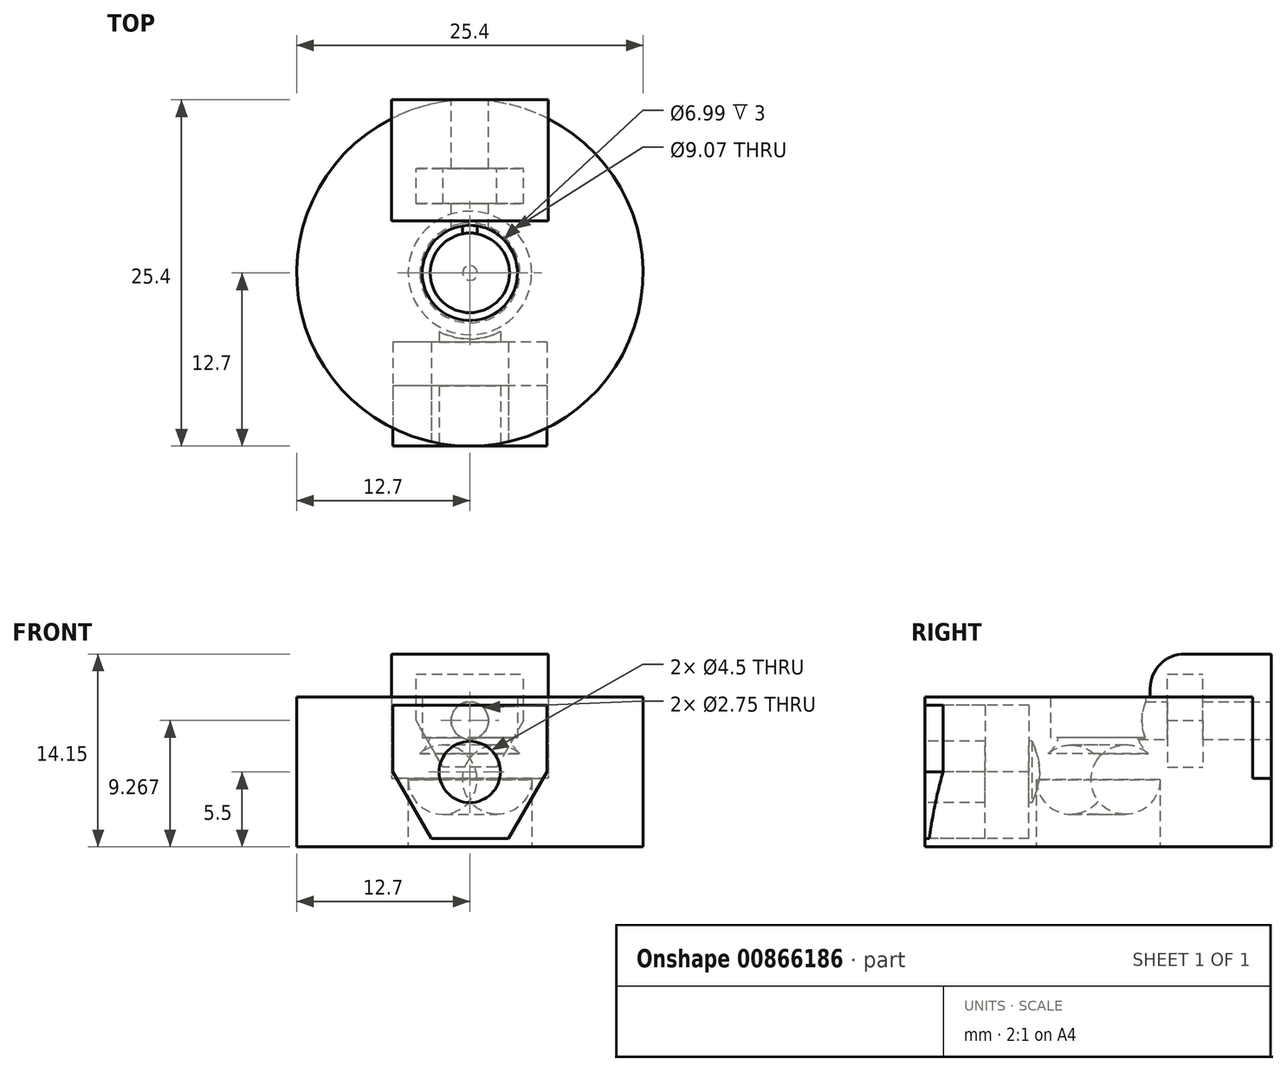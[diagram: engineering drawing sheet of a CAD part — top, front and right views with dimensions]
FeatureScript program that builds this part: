
annotation { "Feature Type Name" : "Feature", "Feature Type Description" : "" }
export const myFeature = defineFeature(function(context is Context, id is Id, definition is map)
    precondition{}
    {
        {
            var Q0;
            Q0=qCreatedBy(makeId("Top.planeOp"),FACE);
            var sketch = newSketch(context, id + "F0", { "sketchPlane" : qUnion([Q0])});
            skCircle(sketch, "E0", {"center": v(0, 0) * mm, "radius": 3.5 * mm});
            skCircle(sketch, "E1", {"center": v(0, 0) * mm, "radius": 12.7 * mm});
            skSolve(sketch);
        }
        {
            var Q0;
            Q0=qSketchRegion(id+"F0",true);
            extrude(context, id + "F1", {"entities" : qUnion([Q0]), "endBound" : BoundingType.SYMMETRIC, "depth" : 11 * mm, "offsetDistance" : 25.4 * mm});
        }
        {
            var Q0;
            Q0=qCreatedBy(makeId("Front.planeOp"),FACE);
            cPlane(context, id + "F2", {"entities" : qUnion([Q0]), "cplaneType" : CPlaneType.OFFSET, "offset" : 12.7 * mm, "width" : 152.4 * mm, "height" : 152.4 * mm});
        }
        {
            var Q0;
            Q0=qCreatedBy(id+"F2.planeOp",FACE);
            var sketch = newSketch(context, id + "F3", { "sketchPlane" : qUnion([Q0])});
            skCircle(sketch, "E2", {"center": v(0, 0) * mm, "radius": 2.25 * mm});
            skSolve(sketch);
        }
        {
            var Q0;
            Q0=makeQuery(id+"F3.imprint","IMPRINT",FACE,{"disambiguationData":[TD([[makeQuery(id+"F3.imprint","IMPRINT",EDGE,{"derivedFrom":sQuery(id+"F3.wireOp",EDGE,"E2")}),1.0]])]});
            extrude(context, id + "F4", {"entities" : qUnion([Q0]), "operationType" : NewBodyOperationType.REMOVE, "oppositeDirection" : true, "depth" : 7.62 * mm, "offsetDistance" : 25.4 * mm});
        }
        {
            var Q0;
            Q0=qCreatedBy(id+"F2.planeOp",FACE);
            var sketch = newSketch(context, id + "F5", { "sketchPlane" : qUnion([Q0])});
            skCircle(sketch, "E3.cCircle", {"center": v(0, 0) * mm, "radius": 4.89 * mm, "construction": true});
            skLineSegment(sketch, "E3.0", {"start": v(2.82, -4.89) * mm, "end": v(-2.82, -4.89) * mm});
            skLineSegment(sketch, "E3.1", {"start": v(-2.82, -4.89) * mm, "end": v(-5.65, 0) * mm});
            skLineSegment(sketch, "E3.2", {"start": v(-5.65, 0) * mm, "end": v(-2.82, 4.89) * mm});
            skLineSegment(sketch, "E3.3", {"start": v(-2.82, 4.89) * mm, "end": v(2.82, 4.89) * mm});
            skLineSegment(sketch, "E3.4", {"start": v(2.82, 4.89) * mm, "end": v(5.65, 0) * mm});
            skLineSegment(sketch, "E3.5", {"start": v(5.65, 0) * mm, "end": v(2.82, -4.89) * mm});
            skPoint(sketch, "E3.0.midPoint", {"position": v(0, -4.89) * mm});
            skLineSegment(sketch, "E4", {"start": v(-2.82, 4.89) * mm, "end": v(-5.65, 4.89) * mm});
            skLineSegment(sketch, "E5", {"start": v(-5.65, 4.89) * mm, "end": v(-5.65, 0) * mm});
            skLineSegment(sketch, "E6.MirrorCS", {"start": v(2.82, 4.89) * mm, "end": v(5.65, 4.89) * mm});
            skLineSegment(sketch, "E7.MirrorCS", {"start": v(5.65, 4.89) * mm, "end": v(5.65, 0) * mm});
            skSolve(sketch);
        }
        {
            var Q0;
            Q0=makeQuery(id+"F5.imprint","IMPRINT",FACE,{"disambiguationData":[TD([[makeQuery(id+"F5.imprint","IMPRINT",EDGE,{"derivedFrom":sQuery(id+"F5.wireOp",EDGE,"E3.2")}),1.0]])]});
            var Q1;
            Q1=makeQuery(id+"F5.imprint","IMPRINT",FACE,{"disambiguationData":[TD([[makeQuery(id+"F5.imprint","IMPRINT",EDGE,{"derivedFrom":sQuery(id+"F5.wireOp",EDGE,"E3.0")}),-1.0]])]});
            var Q2;
            Q2=makeQuery(id+"F5.imprint","IMPRINT",FACE,{"disambiguationData":[TD([[makeQuery(id+"F5.imprint","IMPRINT",EDGE,{"derivedFrom":sQuery(id+"F5.wireOp",EDGE,"E3.4")}),1.0]])]});
            extrude(context, id + "F6", {"entities" : qUnion([Q0, Q1, Q2]), "operationType" : NewBodyOperationType.REMOVE, "oppositeDirection" : true, "depth" : 7.62 * mm, "offsetDistance" : 25.4 * mm});
        }
        {
            var Q0;
            Q0=qSketchRegion(id+"F5",true);
            extrude(context, id + "F7", {"entities" : qUnion([Q0]), "oppositeDirection" : true, "depth" : 7.62 * mm - 3.2 * mm, "offsetDistance" : 25.4 * mm});
        }
        {
            var Q0;
            Q0=qSketchRegion(id+"F3",true);
            extrude(context, id + "F8", {"entities" : qUnion([Q0]), "operationType" : NewBodyOperationType.REMOVE, "oppositeDirection" : true, "depth" : 12.7 * mm, "offsetDistance" : 25.4 * mm});
        }
        {
            var Q0;
            Q0=qCreatedBy(makeId("Top.planeOp"),FACE);
            var sketch = newSketch(context, id + "F9", { "sketchPlane" : qUnion([Q0])});
            skCircle(sketch, "E8", {"center": v(0, 0) * mm, "radius": 2.8 * mm});
            skCircle(sketch, "E9", {"center": v(0, 0) * mm, "radius": 4.85 * mm});
            skSolve(sketch);
        }
        {
            var Q0;
            Q0=makeQuery(id+"F9.imprint","IMPRINT",FACE,{"disambiguationData":[TD([[makeQuery(id+"F9.imprint","IMPRINT",EDGE,{"derivedFrom":sQuery(id+"F9.wireOp",EDGE,"E8")}),-1.0]])]});
            extrude(context, id + "F10", {"entities" : qUnion([Q0]), "operationType" : NewBodyOperationType.ADD, "depth" : 2.5 * mm, "offsetDistance" : 25.4 * mm, "hasSecondDirection" : true, "secondDirectionOppositeDirection" : true, "secondDirectionDepth" : 5.5 * mm});
        }
        {
            var Q0;
            Q0=qCreatedBy(id+"F2.planeOp",FACE);
            cPlane(context, id + "F11", {"entities" : qUnion([Q0]), "cplaneType" : CPlaneType.OFFSET, "offset" : 25.4 * mm, "oppositeDirection" : true, "width" : 152.4 * mm, "height" : 152.4 * mm});
        }
        {
            var Q0;
            Q0=qCreatedBy(id+"F11.planeOp",FACE);
            var sketch = newSketch(context, id + "F12", { "sketchPlane" : qUnion([Q0])});
            skLineSegment(sketch, "E10.bottom", {"start": v(-5.76, 8.65) * mm, "end": v(5.76, 8.65) * mm});
            skLineSegment(sketch, "E10.top", {"start": v(-5.76, -0.48) * mm, "end": v(5.76, -0.48) * mm});
            skLineSegment(sketch, "E10.left", {"start": v(-5.76, 8.65) * mm, "end": v(-5.76, -0.48) * mm});
            skLineSegment(sketch, "E10.right", {"start": v(5.76, 8.65) * mm, "end": v(5.76, -0.48) * mm});
            skPoint(sketch, "E10.middle", {"position": v(0, 4.08) * mm});
            skSolve(sketch);
        }
        {
            var Q0;
            Q0 = qSketchRegion(id + "F12", true);
            extrude(context, id + "F13", {"entities" : qUnion([Q0]), "operationType" : NewBodyOperationType.ADD, "depth" : 8.9 * mm, "offsetDistance" : 25.4 * mm});
        }
        {
            var Q0;
            Q0=makeQuery(id+"F13.opExtrude","CAP_EDGE",EDGE,{"disambiguationData":[OSD([sQuery(id+"F12.wireOp",EDGE,"E10.bottom")])],"isStart":false});
            fillet(context, id + "F14", {"entities" : qUnion([Q0]), "radius" : 2.54 * mm, "tangentPropagation" : true, "allowEdgeOverflow" : false});
        }
        {
            var Q0;
            Q0=qCreatedBy(id+"F11.planeOp",FACE);
            var sketch = newSketch(context, id + "F15", { "sketchPlane" : qUnion([Q0])});
            skCircle(sketch, "E11.cCircle", {"center": v(0, 3.77) * mm, "radius": 3.41 * mm, "construction": true});
            skLineSegment(sketch, "E11.0", {"start": v(1.97, 0.36) * mm, "end": v(-1.97, 0.36) * mm});
            skLineSegment(sketch, "E11.1", {"start": v(-1.97, 0.36) * mm, "end": v(-3.94, 3.77) * mm});
            skLineSegment(sketch, "E11.2", {"start": v(-3.94, 3.77) * mm, "end": v(-1.97, 7.18) * mm});
            skLineSegment(sketch, "E11.3", {"start": v(-1.97, 7.18) * mm, "end": v(1.97, 7.18) * mm});
            skLineSegment(sketch, "E11.4", {"start": v(1.97, 7.18) * mm, "end": v(3.94, 3.77) * mm});
            skLineSegment(sketch, "E11.5", {"start": v(3.94, 3.77) * mm, "end": v(1.97, 0.36) * mm});
            skPoint(sketch, "E11.0.midPoint", {"position": v(0, 0.36) * mm});
            skCircle(sketch, "E12", {"center": v(0, 3.77) * mm, "radius": 1.38 * mm});
            skLineSegment(sketch, "E13", {"start": v(3.94, 3.77) * mm, "end": v(3.94, 7.18) * mm});
            skLineSegment(sketch, "E14", {"start": v(3.94, 7.18) * mm, "end": v(1.97, 7.18) * mm});
            skLineSegment(sketch, "E15.MirrorCS", {"start": v(-3.94, 7.18) * mm, "end": v(-1.97, 7.18) * mm});
            skLineSegment(sketch, "E16.MirrorCS", {"start": v(-3.94, 3.77) * mm, "end": v(-3.94, 7.18) * mm});
            skSolve(sketch);
        }
        {
            var Q0;
            Q0=makeQuery(id+"F15.imprint","IMPRINT",FACE,{"disambiguationData":[TD([[makeQuery(id+"F15.imprint","IMPRINT",EDGE,{"derivedFrom":sQuery(id+"F15.wireOp",EDGE,"E11.2")}),1.0]])]});
            var Q1;
            Q1=makeQuery(id+"F15.imprint","IMPRINT",FACE,{"disambiguationData":[TD([[makeQuery(id+"F15.imprint","IMPRINT",EDGE,{"derivedFrom":sQuery(id+"F15.wireOp",EDGE,"E11.0")}),-1.0]])]});
            var Q2;
            Q2=makeQuery(id+"F15.imprint","IMPRINT",FACE,{"disambiguationData":[TD([[makeQuery(id+"F15.imprint","IMPRINT",EDGE,{"derivedFrom":sQuery(id+"F15.wireOp",EDGE,"E11.4")}),1.0]])]});
            extrude(context, id + "F16", {"entities" : qUnion([Q0, Q1, Q2]), "operationType" : NewBodyOperationType.REMOVE, "depth" : 7.62 * mm, "offsetDistance" : 25.4 * mm});
        }
        {
            var Q0;
            Q0=qSketchRegion(id+"F15",true);
            extrude(context, id + "F17", {"entities" : qUnion([Q0]), "operationType" : NewBodyOperationType.ADD, "depth" : 7.62 * mm - (2.36 * 1.1) * mm, "offsetDistance" : 25.4 * mm});
        }
        {
            var Q0;
            Q0=qCreatedBy(id+"F11.planeOp",FACE);
            var sketch = newSketch(context, id + "F18", { "sketchPlane" : qUnion([Q0])});
            skCircle(sketch, "E17.cCircle", {"center": v(0, 3.77) * mm, "radius": 3.41 * mm, "construction": true});
            skLineSegment(sketch, "E17.0", {"start": v(1.97, 0.36) * mm, "end": v(-1.97, 0.36) * mm});
            skLineSegment(sketch, "E17.1", {"start": v(-1.97, 0.36) * mm, "end": v(-3.94, 3.77) * mm});
            skLineSegment(sketch, "E17.2", {"start": v(-3.94, 3.77) * mm, "end": v(-1.97, 7.18) * mm});
            skLineSegment(sketch, "E17.3", {"start": v(-1.97, 7.18) * mm, "end": v(1.97, 7.18) * mm});
            skLineSegment(sketch, "E17.4", {"start": v(1.97, 7.18) * mm, "end": v(3.94, 3.77) * mm});
            skLineSegment(sketch, "E17.5", {"start": v(3.94, 3.77) * mm, "end": v(1.97, 0.36) * mm});
            skPoint(sketch, "E17.0.midPoint", {"position": v(0, 0.36) * mm});
            skCircle(sketch, "E18", {"center": v(0, 3.77) * mm, "radius": 1.38 * mm});
            skLineSegment(sketch, "E19", {"start": v(3.94, 3.77) * mm, "end": v(3.94, 7.18) * mm});
            skLineSegment(sketch, "E20", {"start": v(3.94, 7.18) * mm, "end": v(1.97, 7.18) * mm});
            skLineSegment(sketch, "E21.MirrorCS", {"start": v(-3.94, 2.89) * mm, "end": v(-1.97, 2.89) * mm});
            skLineSegment(sketch, "E22.MirrorCS", {"start": v(-3.94, -0.52) * mm, "end": v(-3.94, 2.89) * mm});
            skSolve(sketch);
        }
        {
            var Q0;
            Q0=makeQuery(id+"F18.imprint","IMPRINT",FACE,{"disambiguationData":[TD([[makeQuery(id+"F18.imprint","IMPRINT",EDGE,{"derivedFrom":sQuery(id+"F18.wireOp",EDGE,"E18")}),1.0]])]});
            var Q1;
            Q1=sQuery(id+"F18.wireOp",EDGE,"E18");
            extrude(context, id + "F19", {"entities" : qUnion([Q0]), "operationType" : NewBodyOperationType.REMOVE, "surfaceEntities" : qUnion([Q1]), "depth" : 12.7 * mm, "offsetDistance" : 25.4 * mm});
        }
        {
            var Q0;
            Q0=makeQuery(id+"F10.boolean.opBoolean","MERGE",FACE,{"derivedFrom":[makeQuery(id+"F1.opExtrude","CAP_FACE",FACE,{"disambiguationData":[OSD([sQuery(id+"F0.wireOp",EDGE,"E0"),sQuery(id+"F0.wireOp",EDGE,"E1")])],"isStart":true}),makeQuery(id+"F10.opExtrude","CAP_FACE",FACE,{"disambiguationData":[OSD([sQuery(id+"F9.wireOp",EDGE,"E8"),sQuery(id+"F9.wireOp",EDGE,"E9")])],"isStart":true})]});
            var sketch = newSketch(context, id + "F20", { "sketchPlane" : qUnion([Q0])});
            skCircle(sketch, "E23", {"center": v(0, 0) * mm, "radius": 4.53 * mm});
            skSolve(sketch);
        }
        {
            var Q0;
            Q0 = qSketchRegion(id + "F20", true);
            extrude(context, id + "F21", {"entities" : qUnion([Q0]), "operationType" : NewBodyOperationType.REMOVE, "oppositeDirection" : true, "depth" : 6.35 * mm, "offsetDistance" : 25.4 * mm});
        }
        {
            var Q0;
            Q0=makeQuery(id+"F21.boolean.opBoolean","INTERSECT",EDGE,{"derivedFrom":[makeQuery(id+"F10.opExtrude","SWEPT_FACE",FACE,{"disambiguationData":[OSD([sQuery(id+"F9.wireOp",EDGE,"E8")])]}),makeQuery(id+"F21.opExtrude","CAP_FACE",FACE,{"disambiguationData":[OSD([sQuery(id+"F20.wireOp",EDGE,"E23")])],"isStart":false})]});
            fillet(context, id + "F22", {"entities" : qUnion([Q0]), "radius" : 2.54 * mm, "tangentPropagation" : true, "allowEdgeOverflow" : false});
        }
        {
            var Q0;
            {var subQ0=sQuery(id+"F20.wireOp",EDGE,"E23");Q0=makeQuery(id+"F22.opFillet","BLEND_EDGE",EDGE,{"blendedFrom":[makeQuery(id+"F21.boolean.opBoolean","INTERSECT",EDGE,{"derivedFrom":[makeQuery(id+"F10.opExtrude","SWEPT_FACE",FACE,{"disambiguationData":[OSD([sQuery(id+"F9.wireOp",EDGE,"E8")])]}),makeQuery(id+"F21.opExtrude","CAP_FACE",FACE,{"disambiguationData":[OSD([subQ0])],"isStart":false})]}),makeQuery(id+"F21.boolean.opBoolean","COPY",FACE,{"derivedFrom":makeQuery(id+"F21.opExtrude","SWEPT_FACE",FACE,{"disambiguationData":[OSD([subQ0])]})})],"blendedInto":[makeQuery(id+"F21.boolean.opBoolean","COPY",FACE,{"derivedFrom":makeQuery(id+"F21.opExtrude","SWEPT_FACE",FACE,{"disambiguationData":[OSD([subQ0])]})})]});}
            fillet(context, id + "F23", {"entities" : qUnion([Q0]), "radius" : 2.54 * mm, "tangentPropagation" : true, "allowEdgeOverflow" : false});
        }
    });
